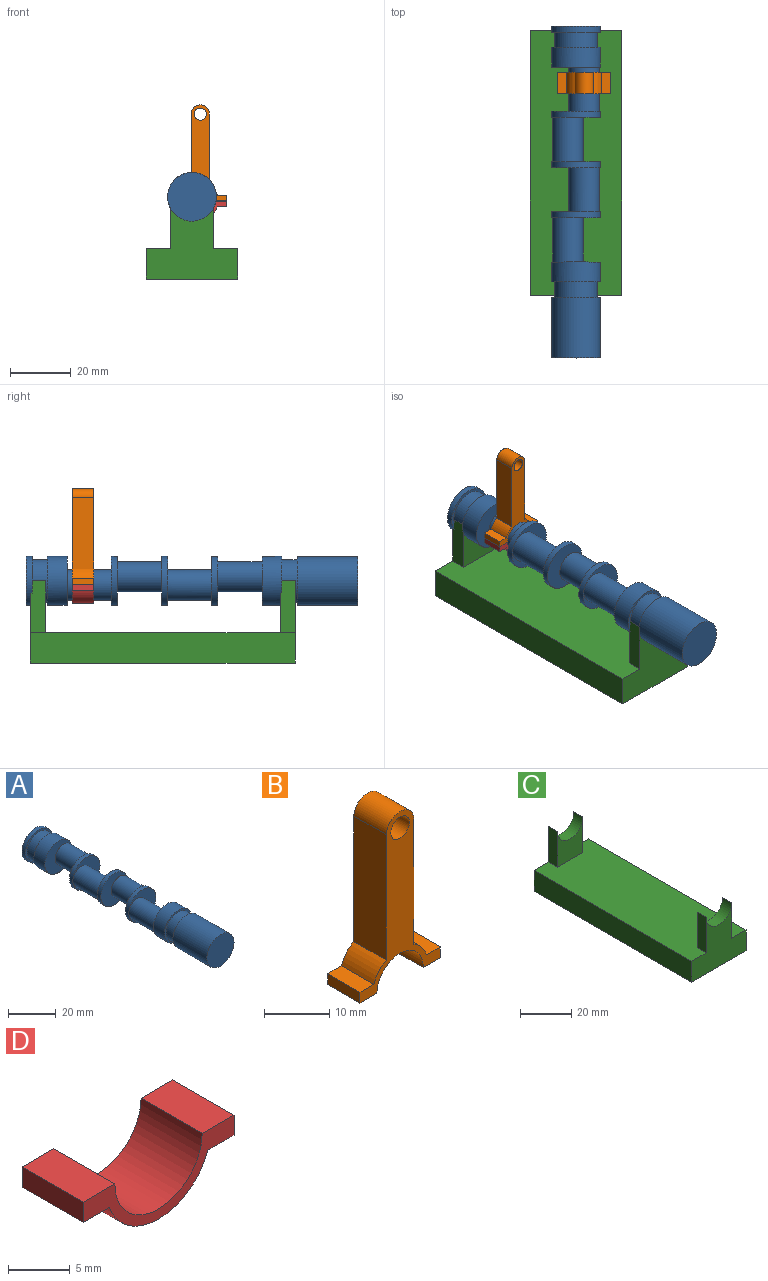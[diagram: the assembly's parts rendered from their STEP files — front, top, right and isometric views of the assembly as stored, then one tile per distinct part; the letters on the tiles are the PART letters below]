
ASSEMBLY  parts=4 mates=7
PART A: 27 faces, bbox 36x129x36 mm
  f0: cylinder r=8mm len=16mm, axis (0,1,0), area 326.7mm2, adj f2,f22
  f1: cylinder r=8mm len=16mm, axis (0,1,0), area 326.7mm2, adj f16,f17
  f2: plane 16x16mm, normal (0,-1,0), area 122.5mm2, adj f0,f3
  f3: cylinder r=5mm len=14.5mm, axis (0,1,0), area 455.5mm2, adj f2,f4
  f4: plane 36x36mm, normal (0,1,0), area 44mm2, adj f3,f5
  f5: cylinder r=8mm len=16mm, axis (0,1,0), area 100.5mm2, adj f4,f6
  f6: plane 16x16mm, normal (0,-1,0), area 122.5mm2, adj f5,f7
  f7: cylinder r=5mm len=14.5mm, axis (0,1,0), area 455.5mm2, adj f6,f8
  f8: plane 16x16mm, normal (0,1,0), area 122.5mm2, adj f7,f9
  f9: cylinder r=8mm len=16mm, axis (0,1,0), area 100.5mm2, adj f8,f10
  f10: plane 16x16mm, normal (0,-1,0), area 122.5mm2, adj f9,f11
  f11: cylinder r=5mm len=14.5mm, axis (0,1,0), area 455.5mm2, adj f10,f12
  f12: plane 36x36mm, normal (0,1,0), area 44mm2, adj f11,f13
  f13: cylinder r=8mm len=16mm, axis (0,1,0), area 100.5mm2, adj f12,f14
  f14: plane 16x16mm, normal (0,-1,0), area 122.5mm2, adj f13,f15
  f15: cylinder r=5mm len=14.5mm, axis (0,1,0), area 455.5mm2, adj f14,f16
  f16: plane 16x16mm, normal (0,1,0), area 122.5mm2, adj f1,f15
  f17: plane 16x16mm, normal (0,-1,0), area 47.1mm2, adj f1,f18
  f18: cylinder r=7mm len=14mm, axis (0,-1,0), area 219.9mm2, adj f17,f21
  f19: cylinder r=8mm len=20mm, axis (0,1,0), area 1005.3mm2, adj f20,f21
  f20: plane 16x16mm, normal (0,-1,0), area 201.1mm2, adj f19
  f21: plane 16x16mm, normal (0,1,0), area 47.1mm2, adj f18,f19
  f22: plane 16x16mm, normal (0,1,0), area 47.1mm2, adj f0,f23
  f23: cylinder r=7mm len=14mm, axis (0,1,0), area 219.9mm2, adj f22,f26
  f24: cylinder r=8mm len=16mm, axis (0,-1,0), area 100.5mm2, adj f25,f26
  f25: plane 16x16mm, normal (0,1,0), area 201.1mm2, adj f24
  f26: plane 16x16mm, normal (0,-1,0), area 47.1mm2, adj f23,f24
PART B: 15 faces, bbox 17.4x7x31.7 mm
  f0: cylinder r=6mm len=7mm, axis (0,1,0), area 29.7mm2, adj f2,f9,f10,f11
  f1: cylinder r=6mm len=7mm, axis (0,1,0), area 31.1mm2, adj f8,f9,f10,f12
  f2: plane 7x3mm, normal (0,0,1), area 21mm2, adj f0,f3,f9,f10
  f3: plane 7x2mm, normal (-1,0,0), area 14mm2, adj f2,f4,f9,f10
  f4: plane 7x3.66mm, normal (0,0,-1), area 25.6mm2, adj f3,f5,f9,f10
  f5: cylinder r=5mm len=10mm, axis (0,1,0), area 111.2mm2, adj f4,f6,f9,f10
  f6: plane 7x3.72mm, normal (0,0,-1), area 26.1mm2, adj f5,f7,f9,f10
  f7: plane 7x2mm, normal (1,0,0), area 14mm2, adj f6,f8,f9,f10
  f8: plane 7x3mm, normal (0,0,1), area 21mm2, adj f1,f7,f9,f10
  f9: plane 31.68x17.38mm, normal (0,-1,0), area 166.7mm2, adj f0,f1,f2,f3,f4,f5,f6,f7
  f10: plane 31.68x17.38mm, normal (0,1,0), area 166.7mm2, adj f0,f1,f2,f3,f4,f5,f6,f7
  f11: plane 23.49x7mm, normal (-1,0,0), area 164.4mm2, adj f0,f9,f10,f14
  f12: plane 23.3x7mm, normal (1,0,0), area 163.1mm2, adj f1,f9,f10,f14
  f13: cylinder r=2mm len=7mm, axis (0,1,0), area 88mm2, adj f9,f10
  f14: cylinder r=3mm len=7mm, axis (0,1,0), area 64.7mm2, adj f9,f10,f11,f12
PART C: 14 faces, bbox 30x87x27 mm
  f0: plane 87x30mm, normal (0,0,1), area 2470mm2, adj f1,f2,f3,f4,f6,f8,f9,f10
  f1: plane 87x10mm, normal (-1,0,0), area 870mm2, adj f0,f2,f4,f5
  f2: plane 30x27mm, normal (0,-1,0), area 461mm2, adj f0,f1,f3,f5,f6,f7,f8
  f3: plane 87x10mm, normal (1,0,0), area 870mm2, adj f0,f2,f4,f5
  f4: plane 30x27mm, normal (0,1,0), area 461mm2, adj f0,f1,f3,f5,f10,f11,f12
  f5: plane 87x30mm, normal (0,0,-1), area 2610mm2, adj f1,f2,f3,f4
  f6: plane 17x5mm, normal (-1,0,0), area 85mm2, adj f0,f2,f7,f9
  f7: cylinder r=7mm len=14mm, axis (0,-1,0), area 110mm2, adj f2,f6,f8,f9
  f8: plane 17x5mm, normal (1,0,0), area 85mm2, adj f0,f2,f7,f9
  f9: plane 17x14mm, normal (0,1,0), area 161mm2, adj f0,f6,f7,f8
  f10: plane 17x5mm, normal (1,0,0), area 85mm2, adj f0,f4,f11,f13
  f11: cylinder r=7mm len=14mm, axis (0,1,0), area 110mm2, adj f4,f10,f12,f13
  f12: plane 17x5mm, normal (-1,0,0), area 85mm2, adj f0,f4,f11,f13
  f13: plane 17x14mm, normal (0,-1,0), area 161mm2, adj f0,f10,f11,f12
PART D: 10 faces, bbox 17.3x7x6 mm
  f0: plane 7x3mm, normal (0,0,-1), area 21mm2, adj f1,f7,f8,f9
  f1: cylinder r=6mm len=11.31mm, axis (0,1,0), area 103.4mm2, adj f0,f2,f8,f9
  f2: plane 7x3mm, normal (0,0,-1), area 21mm2, adj f1,f3,f8,f9
  f3: plane 7x2mm, normal (1,0,0), area 14mm2, adj f2,f4,f8,f9
  f4: plane 7x3.66mm, normal (0,0,1), area 25.6mm2, adj f3,f5,f8,f9
  f5: cylinder r=5mm len=10mm, axis (0,1,0), area 110mm2, adj f4,f6,f8,f9
  f6: plane 7x3.66mm, normal (0,0,1), area 25.6mm2, adj f5,f7,f8,f9
  f7: plane 7x2mm, normal (-1,0,0), area 14mm2, adj f0,f6,f8,f9
  f8: plane 17.31x6mm, normal (0,-1,0), area 28.4mm2, adj f0,f1,f2,f3,f4,f5,f6,f7
  f9: plane 17.31x6mm, normal (0,1,0), area 28.4mm2, adj f0,f1,f2,f3,f4,f5,f6,f7
PLACE A rot(axis=(0,1,0),26.3deg) t=(-143.83,42.97,54.48)mm
PLACE B t=(-141.14,29.75,53.15)mm
PLACE C t=(-143.83,43.57,27.48)mm
PLACE D t=(-141.14,29.75,53.15)mm
MATE planar B.f9 <-> D.f8  axis (0,-1,0) through (-133.92,22.75,54.96)mm
MATE fastened D.f1 <-> B.f0  axis (0,1,0) through (-141.14,26.25,53.15)mm
MATE cylindrical A.f3 <-> D.f1  axis (0,1,0) through (-141.14,31.47,53.15)mm
MATE parallel A.f2 <-> B.f10  axis (0,-1,0) through (-145.56,31.47,55.33)mm
MATE parallel B.f7 <-> D.f3  axis (1,0,0) through (-132.42,26.25,53.96)mm
MATE cylindrical C.f7 <-> A.f0  axis (0,-1,0) through (-143.83,-40.93,54.48)mm
MATE parallel B.f10 <-> A.f2  axis (0,1,0) through (-135.42,29.75,54.96)mm
